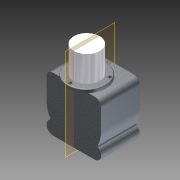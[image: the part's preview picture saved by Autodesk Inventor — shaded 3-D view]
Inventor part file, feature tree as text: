
AUTODESK INVENTOR PART (.ipt)
format: ipt  version: 2016 SP1 (Build 200210100, 210)  size: 174,592 bytes
history: native  units: in
note: dims shown in document units (in); Inventor stores cm internally (conversion verified against a paired STEP export)
features: sketch x5, extrude x4, fillet x3, reference x3, projected_geometry x2, hole x1
ambient origin geometry x8: Origin, YZ Plane, XZ Plane, XY Plane, X Axis, Y Axis, Z Axis, Center Point
bodies: Solid1 (feature_tree)
feature tree (18):
  extrude  "Extrusion1"  Depth=2.11in
  fillet  "Fillet1"  Radius=1.5in
  extrude  "Extrusion2"  Depth=0.5in
  fillet  "Fillet2"  Radius=0.5in
  extrude  "Extrusion3"  Depth=1.055in
  fillet  "Fillet3"  Radius=1.0in
  extrude  "Extrusion4"  Depth=1.5in
  hole  "Hole1"  [1 undecoded]
  sketch  "Sketch1"  dims[d0=2.11in d1=2.11in d2=1.5in d3=0.0in]
  sketch  "Sketch3"  dims[d4=0.25in d8=2.0in d9=0.5in]
  sketch  "Sketch4"  dims[d10=0.5in d12=1.055in d13=1.0in d14=0.0in]
  projected_geometry  "Projected Loop1"
  projected_geometry  "Projected Loop2"
  sketch  "Sketch5"  dims[d15=0.0625in d16=1.5in]
  sketch  "Sketch6"  dims[d17=0.25in d18=0.125in d19=0.0in d20=0.0312in d22=1.0in d23=0.0in d24=0.25in d25=0.129in d26=0.75in d27=0.225in d28=0.25in d29=0.5635in d30=0.25in d31=0.8108in]
  reference  "Reference1"
  reference  "Reference2"
  reference  "Reference3"
note: 1 required parameter value undecoded (feature->parameter linkage not recoverable at this tier; creation-order binding heuristic only, values carry confidence <= 0.55)
